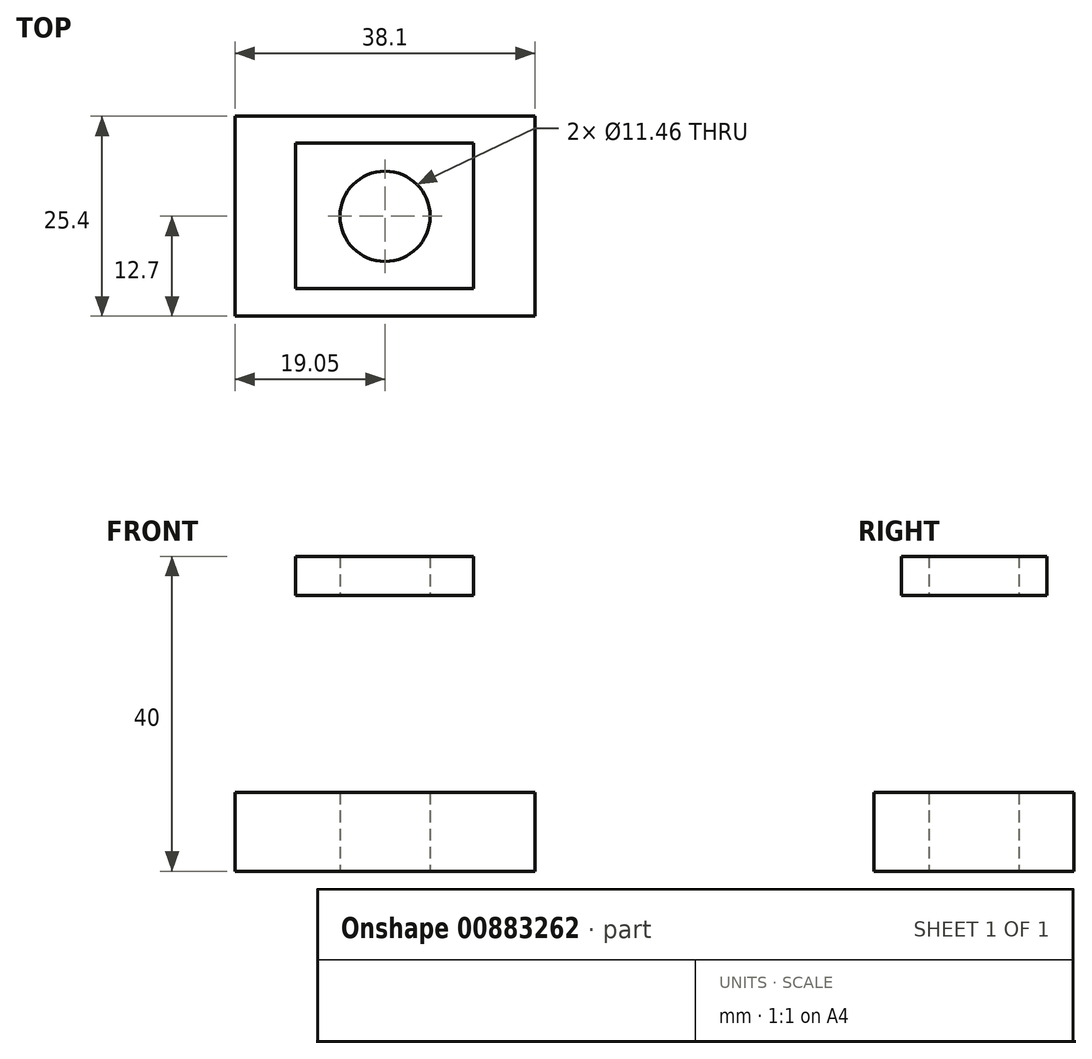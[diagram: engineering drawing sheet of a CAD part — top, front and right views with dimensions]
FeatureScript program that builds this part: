
annotation { "Feature Type Name" : "Feature", "Feature Type Description" : "" }
export const myFeature = defineFeature(function(context is Context, id is Id, definition is map)
    precondition{}
    {
        {
            var Q0;
            Q0=qCreatedBy(makeId("Top.planeOp"),FACE);
            var sketch = newSketch(context, id + "F0", { "sketchPlane" : qUnion([Q0])});
            skLineSegment(sketch, "E0.bottom", {"start": v(19.05, -12.7) * mm, "end": v(-19.05, -12.7) * mm});
            skLineSegment(sketch, "E0.top", {"start": v(19.05, 12.7) * mm, "end": v(-19.05, 12.7) * mm});
            skLineSegment(sketch, "E0.left", {"start": v(19.05, -12.7) * mm, "end": v(19.05, 12.7) * mm});
            skLineSegment(sketch, "E0.right", {"start": v(-19.05, -12.7) * mm, "end": v(-19.05, 12.7) * mm});
            skPoint(sketch, "E0.middle", {"position": v(0, 0) * mm});
            skCircle(sketch, "E1", {"center": v(0, 0) * mm, "radius": 5.73 * mm});
            skSolve(sketch);
        }
        {
            var Q0;
            Q0=makeQuery(id+"F0.imprint","IMPRINT",FACE,{"disambiguationData":[TD([[makeQuery(id+"F0.imprint","IMPRINT",EDGE,{"derivedFrom":sQuery(id+"F0.wireOp",EDGE,"E0.bottom")}),-1.0]])]});
            extrude(context, id + "F1", {"entities" : qUnion([Q0]), "depth" : 10 * mm, "offsetDistance" : 25 * mm});
        }
        {
            var Q0;
            Q0=makeQuery(id+"F1.opExtrude","CAP_FACE",FACE,{"disambiguationData":[OSD([sQuery(id+"F0.wireOp",EDGE,"E0.bottom"),sQuery(id+"F0.wireOp",EDGE,"E0.top"),sQuery(id+"F0.wireOp",EDGE,"E0.left"),sQuery(id+"F0.wireOp",EDGE,"E0.right"),sQuery(id+"F0.wireOp",EDGE,"E1")])],"isStart":false});
            var sketch = newSketch(context, id + "F2", { "sketchPlane" : qUnion([Q0])});
            skLineSegment(sketch, "E2.bottom", {"start": v(-15, -12.7) * mm, "end": v(-10, -12.7) * mm});
            skLineSegment(sketch, "E2.top", {"start": v(-15, 12.7) * mm, "end": v(-10, 12.7) * mm});
            skLineSegment(sketch, "E2.left", {"start": v(-15, -12.7) * mm, "end": v(-15, 12.7) * mm});
            skLineSegment(sketch, "E2.right", {"start": v(-10, -12.7) * mm, "end": v(-10, 12.7) * mm});
            skLineSegment(sketch, "E3", {"start": v(-2.46, 12.7) * mm, "end": v(-2.46, -12.7) * mm});
            skLineSegment(sketch, "E4", {"start": v(2.54, 12.7) * mm, "end": v(2.54, -12.7) * mm});
            skPoint(sketch, "E5", {"position": v(0, 0) * mm});
            skLineSegment(sketch, "E6", {"start": v(0, 12.7) * mm, "end": v(0, -14.39) * mm, "construction": true});
            skPoint(sketch, "E6.endSnap0", {"position": v(0, -12.7) * mm});
            skSolve(sketch);
        }
        {
            var Q0;
            {var subQ0=makeQuery(id+"F1.opExtrude","CAP_EDGE",EDGE,{"disambiguationData":[OSD([sQuery(id+"F0.wireOp",EDGE,"E0.left")])],"isStart":false});Q0=makeQuery(id+"F2.imprint","IMPRINT",FACE,{"disambiguationData":[TD([[makeQuery(id+"F2.imprint","IMPRINT",EDGE,{"derivedFrom":subQ0}),1.0]])]});}
            cPlane(context, id + "F3", {"entities" : qUnion([Q0]), "cplaneType" : CPlaneType.OFFSET, "offset" : 25 * mm, "width" : 150 * mm, "height" : 150 * mm});
        }
        {
            var Q0;
            Q0=qCreatedBy(id+"F3.planeOp",FACE);
            var sketch = newSketch(context, id + "F4", { "sketchPlane" : qUnion([Q0])});
            skLineSegment(sketch, "E7.bottom", {"start": v(-11.4, 9.3) * mm, "end": v(11.26, 9.3) * mm});
            skLineSegment(sketch, "E7.top", {"start": v(-11.4, -9.18) * mm, "end": v(11.26, -9.18) * mm});
            skLineSegment(sketch, "E7.left", {"start": v(-11.4, 9.3) * mm, "end": v(-11.4, -9.18) * mm});
            skLineSegment(sketch, "E7.right", {"start": v(11.26, 9.3) * mm, "end": v(11.26, -9.18) * mm});
            skCircle(sketch, "E8.0", {"center": v(0, 0) * mm, "radius": 5.73 * mm});
            skSolve(sketch);
        }
        {
            var Q0;
            Q0=makeQuery(id+"F4.imprint","IMPRINT",FACE,{"disambiguationData":[TD([[makeQuery(id+"F4.imprint","IMPRINT",EDGE,{"derivedFrom":sQuery(id+"F4.wireOp",EDGE,"E7.bottom")}),-1.0]])]});
            extrude(context, id + "F5", {"entities" : qUnion([Q0]), "depth" : 5 * mm, "offsetDistance" : 25 * mm});
        }
    });
